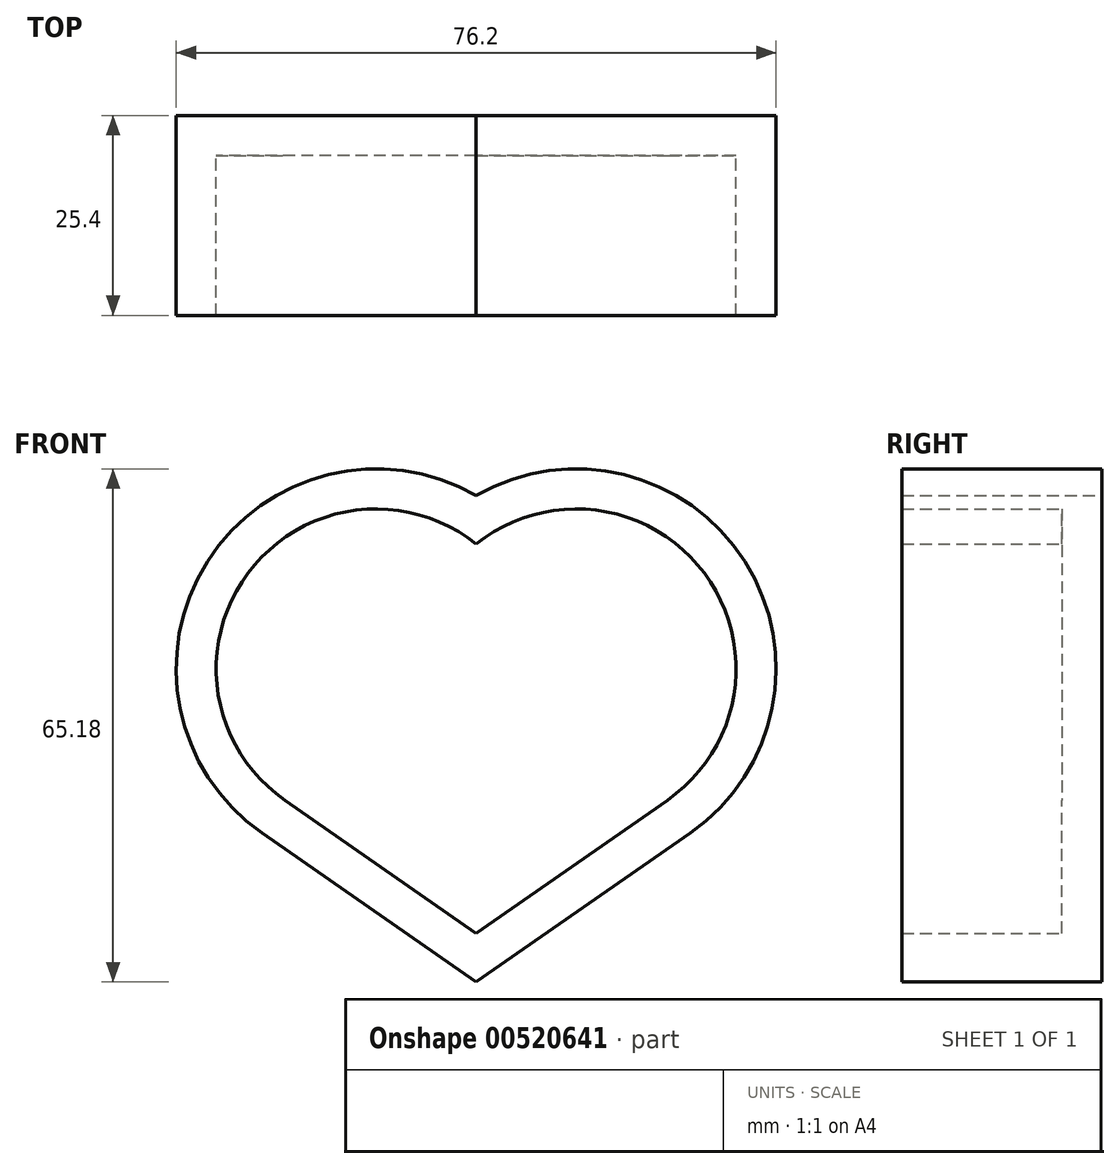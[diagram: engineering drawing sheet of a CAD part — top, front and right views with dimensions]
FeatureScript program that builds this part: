
annotation { "Feature Type Name" : "Feature", "Feature Type Description" : "" }
export const myFeature = defineFeature(function(context is Context, id is Id, definition is map)
    precondition{}
    {
        {
            var Q0;
            Q0=qCreatedBy(makeId("Front.planeOp"),FACE);
            var sketch = newSketch(context, id + "F0", { "sketchPlane" : qUnion([Q0])});
            skCircle(sketch, "E0", {"center": v(0, 0) * mm, "radius": 25.4 * mm});
            skCircle(sketch, "E1", {"center": v(25.4, 0) * mm, "radius": 25.4 * mm});
            skPoint(sketch, "E2", {"position": v(12.7, -22) * mm});
            skLineSegment(sketch, "E3", {"start": v(12.7, -22) * mm, "end": v(12.7, -39.78) * mm});
            skLineSegment(sketch, "E4", {"start": v(12.7, -39.78) * mm, "end": v(-14.5, -20.85) * mm});
            skLineSegment(sketch, "E5", {"start": v(12.7, -39.78) * mm, "end": v(39.9, -20.85) * mm});
            skSolve(sketch);
        }
        {
            var Q0;
            {var subQ5=sQuery(id+"F0.wireOp",EDGE,"VGXMVorV-Bhka-XHRI-ycMi-C0qwzemh4LBb");Q0=makeQuery(id+"F0.imprint","IMPRINT",FACE,{"disambiguationData":[TD([[makeQuery(id+"F0.imprint","IMPRINT",EDGE,{"derivedFrom":subQ5}),1.0]])]});}
            var Q1;
            {var subQ0=sQuery(id+"F0.wireOp",EDGE,"XMDcBOJK-KxLS-55VM-hwmy-Po1coEzqak9t");var subQ1=sQuery(id+"F0.wireOp",EDGE,"E0");var subQ2=makeQuery(id+"F0.imprint","INTERSECT",VERTEX,{"disambiguationData":[OD(0.0)],"derivedFrom":[subQ1,subQ0]});Q1=makeQuery(id+"F0.imprint","IMPRINT",FACE,{"disambiguationData":[TD([[makeQuery(id+"F0.imprint","IMPRINT",EDGE,{"disambiguationData":[TD([[subQ2,1.0]])],"derivedFrom":subQ1}),1.0]])]});}
            var Q2;
            {var subQ0=sQuery(id+"F0.wireOp",EDGE,"E1");var subQ1=sQuery(id+"F0.wireOp",EDGE,"E0");var subQ2=makeQuery(id+"F0.imprint","INTERSECT",VERTEX,{"disambiguationData":[OD(0.0)],"derivedFrom":[subQ1,subQ0]});Q2=makeQuery(id+"F0.imprint","IMPRINT",FACE,{"disambiguationData":[TD([[makeQuery(id+"F0.imprint","IMPRINT",EDGE,{"disambiguationData":[TD([[subQ2,1.0]])],"derivedFrom":subQ1}),-1.0]])]});}
            var Q3;
            {var subQ0=sQuery(id+"F0.wireOp",EDGE,"E1");var subQ1=sQuery(id+"F0.wireOp",EDGE,"E0");var subQ2=makeQuery(id+"F0.imprint","INTERSECT",VERTEX,{"disambiguationData":[OD(0.0)],"derivedFrom":[subQ1,subQ0]});Q3=makeQuery(id+"F0.imprint","IMPRINT",FACE,{"disambiguationData":[TD([[makeQuery(id+"F0.imprint","IMPRINT",EDGE,{"disambiguationData":[TD([[subQ2,1.0]])],"derivedFrom":subQ1}),1.0]])]});}
            extrude(context, id + "F1", {"entities" : qUnion([Q0, Q1, Q2, Q3]), "depth" : 19.05 * mm, "offsetDistance" : 25.4 * mm});
        }
        {
            var Q0;
            Q0 = qSketchRegion(id + "F0", true);
            extrude(context, id + "F2", {"entities" : qUnion([Q0]), "operationType" : NewBodyOperationType.ADD, "depth" : 25.4 * mm, "offsetDistance" : 25.4 * mm});
        }
        {
            var Q0;
            {var subQ0=sQuery(id+"F0.wireOp",EDGE,"E1");Q0=makeQuery(id+"F2.boolean.opBoolean","MERGE",FACE,{"derivedFrom":[makeQuery(id+"F1.opExtrude","CAP_FACE",FACE,{"disambiguationData":[OSD([subQ0])],"isStart":false}),makeQuery(id+"F2.opExtrude","CAP_FACE",FACE,{"disambiguationData":[OSD([sQuery(id+"F0.wireOp",EDGE,"E0"),subQ0,sQuery(id+"F0.wireOp",EDGE,"OXKECsw6-qzDR-UwYy-lfiD-pWS6aNyRJVsG"),sQuery(id+"F0.wireOp",EDGE,"HVifoqcJ-uWbk-VONl-O8da-HVJTIA4F86Vp")])],"isStart":false})]});}
            var Q1;
            Q1=makeQuery(id+"F2.opExtrude","CAP_FACE",FACE,{"disambiguationData":[OSD([sQuery(id+"F0.wireOp",EDGE,"E0"),sQuery(id+"F0.wireOp",EDGE,"E1"),sQuery(id+"F0.wireOp",EDGE,"OXKECsw6-qzDR-UwYy-lfiD-pWS6aNyRJVsG"),sQuery(id+"F0.wireOp",EDGE,"HVifoqcJ-uWbk-VONl-O8da-HVJTIA4F86Vp")])],"isStart":false});
            shell(context, id + "F3", {"entities" : qUnion([Q0, Q1]), "thickness" : 5.08 * mm});
        }
    });
